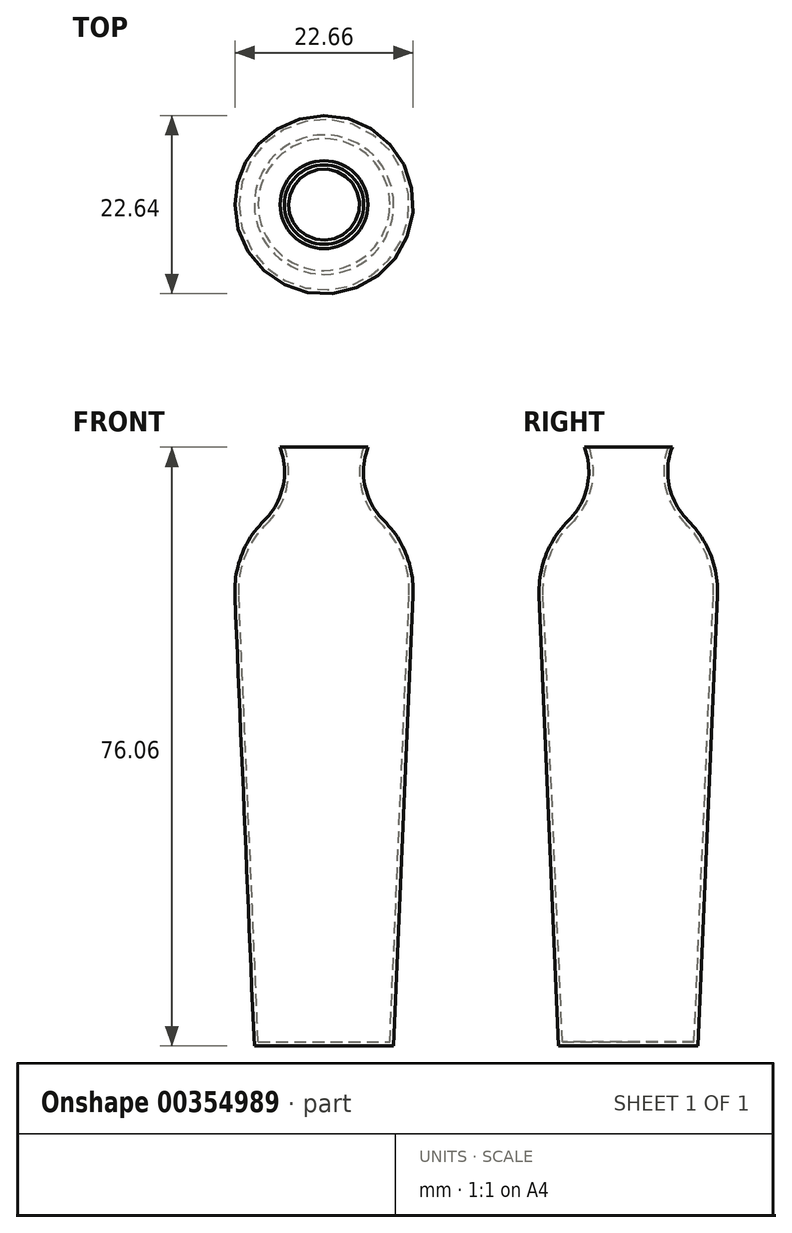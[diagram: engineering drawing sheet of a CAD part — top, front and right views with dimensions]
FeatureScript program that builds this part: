
annotation { "Feature Type Name" : "Feature", "Feature Type Description" : "" }
export const myFeature = defineFeature(function(context is Context, id is Id, definition is map)
    precondition{}
    {
        {
            var Q0;
            Q0=qCreatedBy(makeId("Front.planeOp"),FACE);
            var sketch = newSketch(context, id + "F0", { "sketchPlane" : qUnion([Q0])});
            skLineSegment(sketch, "E0", {"start": v(0, -18.34) * mm, "end": v(-8.85, -18.34) * mm});
            skLineSegment(sketch, "E1", {"start": v(-8.85, -18.34) * mm, "end": v(-11.32, 38.92) * mm});
            skArc(sketch, "E2", {"start": v(-11.32, 38.92) * mm, "mid": v(-10.46, 44.06) * mm, "end": v(-7.6, 48.41) * mm});
            skArc(sketch, "E3", {"start": v(-7.6, 48.41) * mm, "mid": v(-5.2, 52.77) * mm, "end": v(-5.58, 57.72) * mm});
            skLineSegment(sketch, "E4", {"start": v(-5.58, 57.72) * mm, "end": v(-5.04, 57.72) * mm});
            skArc(sketch, "E5.0", {"start": v(-7.24, 48.05) * mm, "mid": v(-4.73, 52.56) * mm, "end": v(-5.04, 57.72) * mm});
            skArc(sketch, "E5.1", {"start": v(-10.81, 38.94) * mm, "mid": v(-9.99, 43.87) * mm, "end": v(-7.24, 48.05) * mm});
            skLineSegment(sketch, "E5.2", {"start": v(-8.37, -17.84) * mm, "end": v(-10.81, 38.94) * mm});
            skLineSegment(sketch, "E5.3", {"start": v(0, -17.84) * mm, "end": v(-8.37, -17.84) * mm});
            skPoint(sketch, "E6.orphan", {"position": v(0, 57.72) * mm});
            skLineSegment(sketch, "E7", {"start": v(0, -17.84) * mm, "end": v(0, -18.34) * mm});
            skLineSegment(sketch, "E8", {"start": v(0, -21.88) * mm, "end": v(0, -17.84) * mm});
            skSolve(sketch);
        }
        {
            var Q0;
            Q0=makeQuery(id+"F0.imprint","IMPRINT",FACE,{"disambiguationData":[TD([[makeQuery(id+"F0.imprint","IMPRINT",EDGE,{"derivedFrom":sQuery(id+"F0.wireOp",EDGE,"E0")}),-1.0]])]});
            var Q1;
            Q1=sQuery(id+"F0.wireOp",EDGE,"E8");
            revolve(context, id + "F1", {"entities" : qUnion([Q0]), "axis" : qUnion([Q1]), "revolveType" : RevolveType.FULL});
        }
    });
